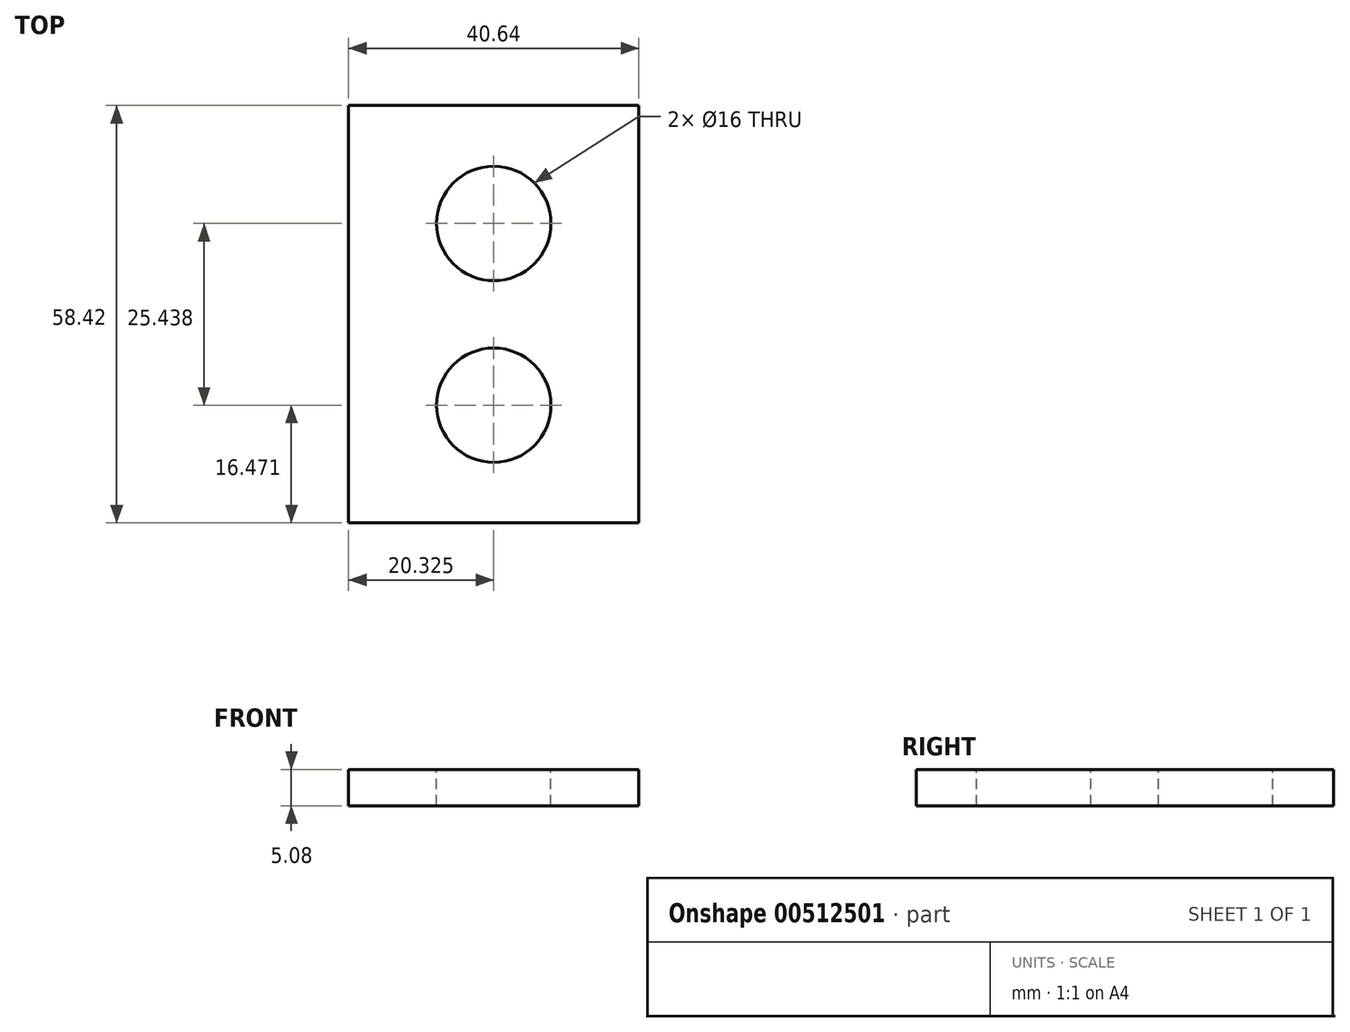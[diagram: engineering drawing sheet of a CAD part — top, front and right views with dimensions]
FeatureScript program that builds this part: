
annotation { "Feature Type Name" : "Feature", "Feature Type Description" : "" }
export const myFeature = defineFeature(function(context is Context, id is Id, definition is map)
    precondition{}
    {
        {
            var Q0;
            Q0=qCreatedBy(makeId("Top.planeOp"),FACE);
            var sketch = newSketch(context, id + "F0", { "sketchPlane" : qUnion([Q0])});
            skLineSegment(sketch, "E0.bottom", {"start": v(-37.06, -28.6) * mm, "end": v(3.58, -28.6) * mm});
            skLineSegment(sketch, "E0.top", {"start": v(-37.06, 29.83) * mm, "end": v(3.58, 29.83) * mm});
            skLineSegment(sketch, "E0.left", {"start": v(-37.06, -28.6) * mm, "end": v(-37.06, 29.83) * mm});
            skLineSegment(sketch, "E0.right", {"start": v(3.58, -28.6) * mm, "end": v(3.58, 29.83) * mm});
            skSolve(sketch);
        }
        {
            var Q0;
            Q0=makeQuery(id+"F0.imprint","IMPRINT",FACE,{"disambiguationData":[TD([[makeQuery(id+"F0.imprint","IMPRINT",EDGE,{"derivedFrom":sQuery(id+"F0.wireOp",EDGE,"E0.bottom")}),1.0]])]});
            extrude(context, id + "F1", {"entities" : qUnion([Q0]), "depth" : 5.08 * mm});
        }
        {
            var Q0;
            Q0=makeQuery(id+"F1.opExtrude","CAP_FACE",FACE,{"disambiguationData":[OSD([sQuery(id+"F0.wireOp",EDGE,"E0.bottom"),sQuery(id+"F0.wireOp",EDGE,"E0.top"),sQuery(id+"F0.wireOp",EDGE,"E0.left"),sQuery(id+"F0.wireOp",EDGE,"E0.right")])],"isStart":false});
            var sketch = newSketch(context, id + "F2", { "sketchPlane" : qUnion([Q0])});
            skCircle(sketch, "E1", {"center": v(-16.74, 13.32) * mm, "radius": 8 * mm});
            skPoint(sketch, "E1.centerSnap0", {"position": v(-16.74, 29.83) * mm});
            skCircle(sketch, "E2", {"center": v(-16.74, -12.12) * mm, "radius": 8 * mm});
            skSolve(sketch);
        }
        {
            var Q0;
            Q0=makeQuery(id+"F2.imprint","IMPRINT",FACE,{"disambiguationData":[TD([[makeQuery(id+"F2.imprint","IMPRINT",EDGE,{"derivedFrom":sQuery(id+"F2.wireOp",EDGE,"E1")}),1.0]])]});
            var Q1;
            Q1=makeQuery(id+"F2.imprint","IMPRINT",FACE,{"disambiguationData":[TD([[makeQuery(id+"F2.imprint","IMPRINT",EDGE,{"derivedFrom":sQuery(id+"F2.wireOp",EDGE,"E2")}),1.0]])]});
            extrude(context, id + "F3", {"entities" : qUnion([Q0, Q1]), "operationType" : NewBodyOperationType.REMOVE, "oppositeDirection" : true, "depth" : 25.4 * mm});
        }
    });
